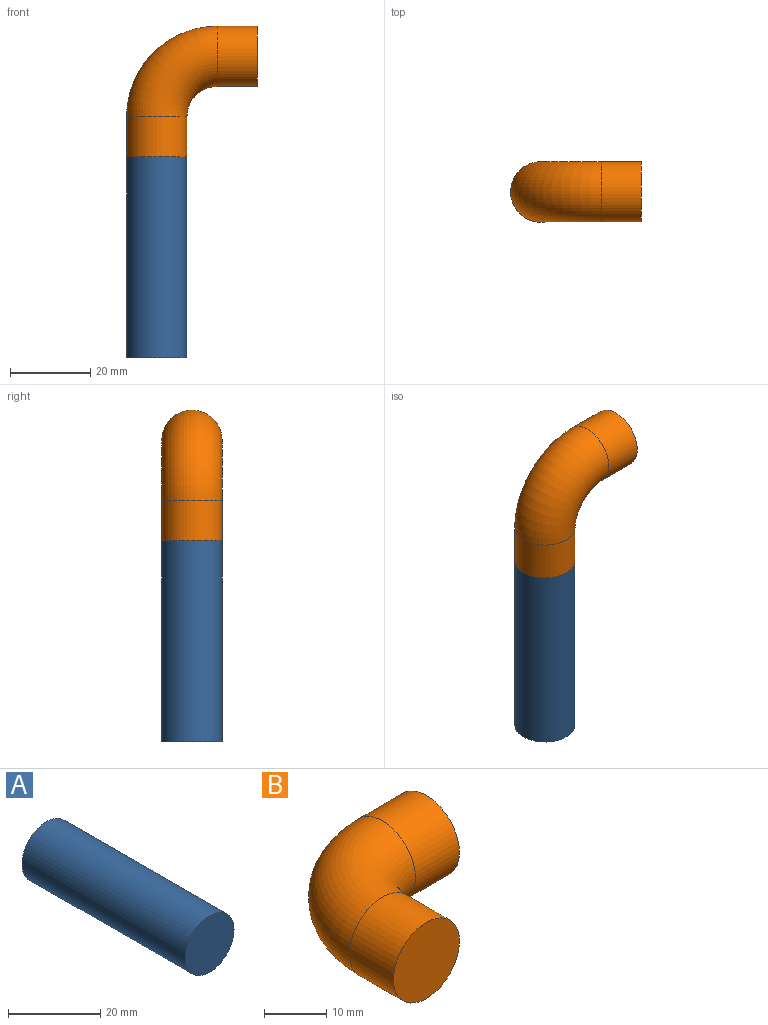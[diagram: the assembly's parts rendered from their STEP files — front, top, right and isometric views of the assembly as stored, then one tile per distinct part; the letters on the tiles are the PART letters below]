
ASSEMBLY  parts=2 mates=1
PART A: 3 faces, bbox 15x50x15 mm
  f0: cylinder r=7.5mm len=50mm, axis (0,1,0), area 2356.2mm2, adj f1,f2
  f1: plane 15x15mm, normal (0,-1,0), area 176.7mm2, adj f0
  f2: plane 15x15mm, normal (0,1,0), area 176.7mm2, adj f0
PART B: 5 faces, bbox 34.4x34.4x15 mm
  f0: plane 15x15mm, normal (0,-1,0), area 176.7mm2, adj f2
  f1: plane 15x15mm, normal (1,0,0), area 176.7mm2, adj f4
  f2: cylinder r=7.5mm len=15mm, axis (0,1,0), area 471.2mm2, adj f0,f3
  f3: torus R=15mm, axis (0,0,-1), area 1110.3mm2, adj f2,f4
  f4: cylinder r=7.5mm len=15mm, axis (1,0,0), area 471.2mm2, adj f1,f3
PLACE A rot(axis=(-1,0,0),90deg) t=(1165,4110,0)mm
PLACE B rot(axis=(-0.58,0.58,0.58),120deg) t=(1190,4110,75)mm
MATE revolute B.f4 <-> A.f0  axis (0,0,-1) through (1165,4110,50)mm
